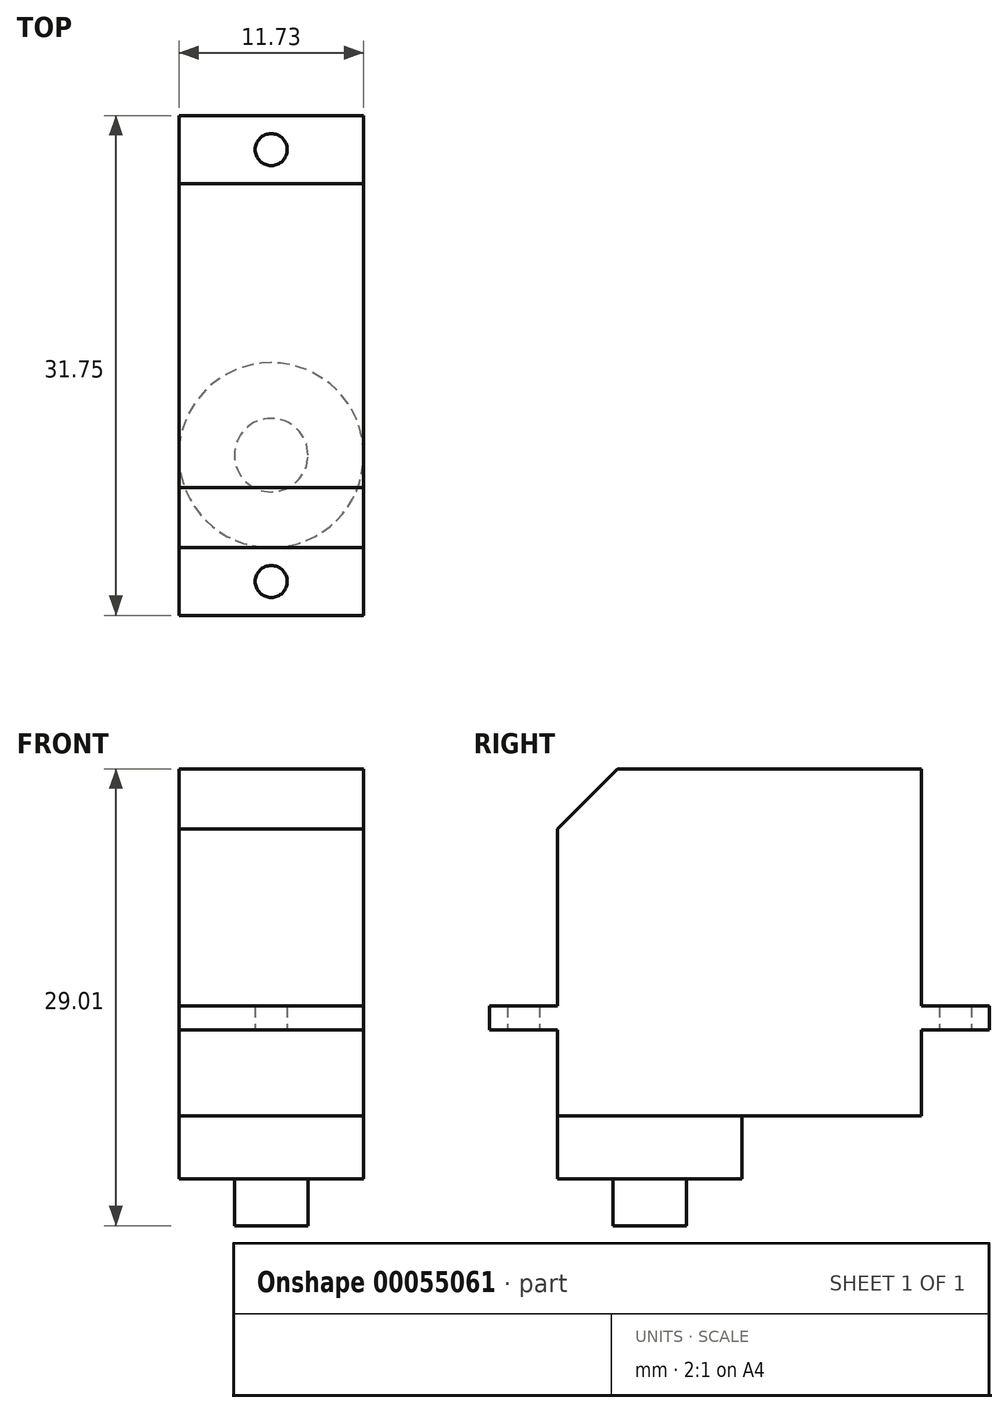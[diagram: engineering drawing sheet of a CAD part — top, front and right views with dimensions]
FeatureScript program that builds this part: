
annotation { "Feature Type Name" : "Feature", "Feature Type Description" : "" }
export const myFeature = defineFeature(function(context is Context, id is Id, definition is map)
    precondition{}
    {
        {
            var Q0;
            Q0=qCreatedBy(makeId("Right.planeOp"),FACE);
            var sketch = newSketch(context, id + "F0", { "sketchPlane" : qUnion([Q0])});
            skLineSegment(sketch, "E0", {"start": v(0, 0) * mm, "end": v(-19.3, 0) * mm});
            skLineSegment(sketch, "E1", {"start": v(-19.3, 0) * mm, "end": v(-23.11, -3.81) * mm});
            skLineSegment(sketch, "E2", {"start": v(-23.11, -3.81) * mm, "end": v(-23.11, -15.04) * mm});
            skLineSegment(sketch, "E3", {"start": v(-23.11, -15.04) * mm, "end": v(-27.43, -15.04) * mm});
            skLineSegment(sketch, "E4", {"start": v(-27.43, -15.04) * mm, "end": v(-27.43, -16.56) * mm});
            skLineSegment(sketch, "E5", {"start": v(-27.43, -16.56) * mm, "end": v(-23.11, -16.56) * mm});
            skLineSegment(sketch, "E6", {"start": v(-23.11, -16.56) * mm, "end": v(-23.11, -22.05) * mm});
            skLineSegment(sketch, "E7", {"start": v(-23.11, -22.05) * mm, "end": v(0, -22.05) * mm});
            skLineSegment(sketch, "E8", {"start": v(0, -22.05) * mm, "end": v(0, -16.56) * mm});
            skLineSegment(sketch, "E9", {"start": v(0, -16.56) * mm, "end": v(4.32, -16.56) * mm});
            skLineSegment(sketch, "E10", {"start": v(4.32, -16.56) * mm, "end": v(4.32, -15.04) * mm});
            skLineSegment(sketch, "E11", {"start": v(4.32, -15.04) * mm, "end": v(0, -15.04) * mm});
            skLineSegment(sketch, "E12", {"start": v(0, -15.04) * mm, "end": v(0, 0) * mm});
            skSolve(sketch);
        }
        {
            var Q0;
            Q0 = qSketchRegion(id + "F0", true);
            extrude(context, id + "F1", {"entities" : qUnion([Q0]), "depth" : 11.73 * mm});
        }
        {
            var Q0;
            Q0=makeQuery(id+"F1.opExtrude","SWEPT_FACE",FACE,{"disambiguationData":[OSD([sQuery(id+"F0.wireOp",EDGE,"E7")])]});
            var sketch = newSketch(context, id + "F2", { "sketchPlane" : qUnion([Q0])});
            skCircle(sketch, "E13", {"center": v(5.87, 17.25) * mm, "radius": 5.87 * mm});
            skPoint(sketch, "E14", {"position": v(5.87, 23.11) * mm});
            skSolve(sketch);
        }
        {
            var Q0;
            {var subQ0=sQuery(id+"F2.wireOp",EDGE,"E13");var subQ1=sQuery(id+"F0.wireOp",EDGE,"E7");var subQ2=makeQuery(id+"F2.imprint","INTERSECT",VERTEX,{"derivedFrom":[makeQuery(id+"F1.opExtrude","CAP_EDGE",EDGE,{"disambiguationData":[OSD([subQ1])],"isStart":true}),subQ0]});Q0=makeQuery(id+"F2.imprint","IMPRINT",FACE,{"disambiguationData":[TD([[makeQuery(id+"F2.imprint","IMPRINT",EDGE,{"disambiguationData":[TD([[subQ2,-1.0]])],"derivedFrom":subQ0}),1.0]])]});}
            extrude(context, id + "F3", {"entities" : qUnion([Q0]), "operationType" : NewBodyOperationType.ADD, "depth" : 4 * mm});
        }
        {
            var Q0;
            Q0=makeQuery(id+"F3.opExtrude","CAP_FACE",FACE,{"disambiguationData":[OSD([sQuery(id+"F2.wireOp",EDGE,"E13")])],"isStart":false});
            var sketch = newSketch(context, id + "F4", { "sketchPlane" : qUnion([Q0])});
            skCircle(sketch, "E15", {"center": v(5.87, 17.25) * mm, "radius": 2.33 * mm});
            skSolve(sketch);
        }
        {
            var Q0;
            Q0=makeQuery(id+"F4.imprint","IMPRINT",FACE,{"disambiguationData":[TD([[makeQuery(id+"F4.imprint","IMPRINT",EDGE,{"derivedFrom":sQuery(id+"F4.wireOp",EDGE,"E15")}),1.0]])]});
            extrude(context, id + "F5", {"entities" : qUnion([Q0]), "operationType" : NewBodyOperationType.ADD, "depth" : 2.97 * mm});
        }
        {
            var Q0;
            Q0=makeQuery(id+"F1.opExtrude","SWEPT_FACE",FACE,{"disambiguationData":[OSD([sQuery(id+"F0.wireOp",EDGE,"E5")])]});
            var sketch = newSketch(context, id + "F6", { "sketchPlane" : qUnion([Q0])});
            skCircle(sketch, "E16", {"center": v(5.87, 25.27) * mm, "radius": 1.02 * mm});
            skCircle(sketch, "E17", {"center": v(5.87, -2.16) * mm, "radius": 1.02 * mm});
            skPoint(sketch, "E18", {"position": v(5.87, 27.43) * mm});
            skPoint(sketch, "E19", {"position": v(0, 25.27) * mm});
            skPoint(sketch, "E20", {"position": v(0, -2.16) * mm});
            skSolve(sketch);
        }
        {
            var Q0;
            Q0 = qSketchRegion(id + "F6", true);
            extrude(context, id + "F7", {"entities" : qUnion([Q0]), "operationType" : NewBodyOperationType.REMOVE, "oppositeDirection" : true, "depth" : 25.4 * mm});
        }
    });
